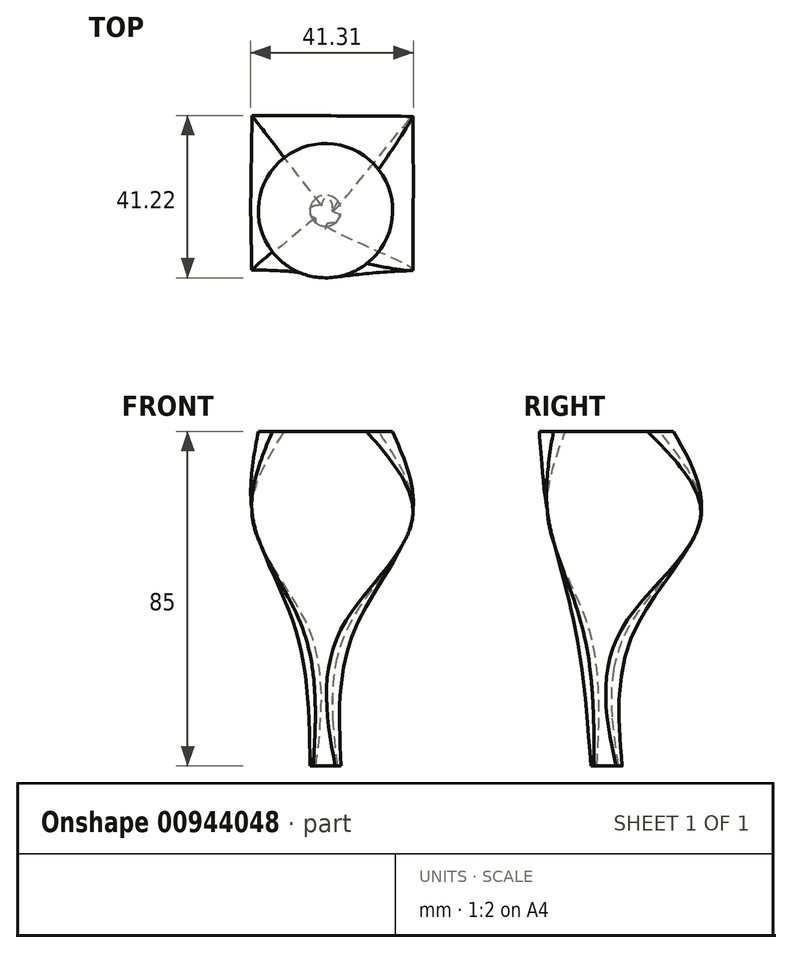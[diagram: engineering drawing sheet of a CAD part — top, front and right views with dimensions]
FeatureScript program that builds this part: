
annotation { "Feature Type Name" : "Feature", "Feature Type Description" : "" }
export const myFeature = defineFeature(function(context is Context, id is Id, definition is map)
    precondition{}
    {
        {
            var Q0;
            Q0=qCreatedBy(makeId("Top.planeOp"),FACE);
            var sketch = newSketch(context, id + "F0", { "sketchPlane" : qUnion([Q0])});
            skCircle(sketch, "E0", {"center": v(0, 0) * mm, "radius": 3.96 * mm});
            skSolve(sketch);
        }
        {
            var Q0;
            Q0=qCreatedBy(makeId("Top.planeOp"),FACE);
            cPlane(context, id + "F1", {"entities" : qUnion([Q0]), "cplaneType" : CPlaneType.OFFSET, "offset" : 85 * mm, "width" : 150 * mm, "height" : 150 * mm});
        }
        {
            var Q0;
            Q0=qCreatedBy(id+"F1.planeOp",FACE);
            var sketch = newSketch(context, id + "F2", { "sketchPlane" : qUnion([Q0])});
            skCircle(sketch, "E1", {"center": v(0, 0) * mm, "radius": 17.07 * mm});
            skSolve(sketch);
        }
        {
            var Q0;
            Q0=qCreatedBy(id+"F1.planeOp",FACE);
            cPlane(context, id + "F3", {"entities" : qUnion([Q0]), "cplaneType" : CPlaneType.OFFSET, "offset" : 20 * mm, "oppositeDirection" : true, "width" : 150 * mm, "height" : 150 * mm});
        }
        {
            var Q0;
            Q0=qCreatedBy(id+"F1.planeOp",FACE);
            cPlane(context, id + "F4", {"entities" : qUnion([Q0]), "cplaneType" : CPlaneType.OFFSET, "offset" : 48.2 * mm, "oppositeDirection" : true, "width" : 150 * mm, "height" : 150 * mm});
        }
        {
            var Q0;
            Q0=qCreatedBy(id+"F4.planeOp",FACE);
            var sketch = newSketch(context, id + "F5", { "sketchPlane" : qUnion([Q0])});
            skCircle(sketch, "E2", {"center": v(0, 0) * mm, "radius": 8.32 * mm});
            skSolve(sketch);
        }
        {
            var Q0;
            Q0=qCreatedBy(id+"F3.planeOp",FACE);
            var sketch = newSketch(context, id + "F6", { "sketchPlane" : qUnion([Q0])});
            skLineSegment(sketch, "E3", {"start": v(-18.72, 24.15) * mm, "end": v(-18.72, -15.03) * mm});
            skLineSegment(sketch, "E4", {"start": v(-18.72, -15.03) * mm, "end": v(22.2, -15.03) * mm});
            skLineSegment(sketch, "E5", {"start": v(22.2, -15.03) * mm, "end": v(22.2, 23.95) * mm});
            skLineSegment(sketch, "E6", {"start": v(22.2, 23.95) * mm, "end": v(-18.72, 24.15) * mm});
            skSolve(sketch);
        }
        {
            var Q0;
            Q0=makeQuery(id+"F0.imprint","IMPRINT",FACE,{"disambiguationData":[TD([[makeQuery(id+"F0.imprint","IMPRINT",EDGE,{"derivedFrom":sQuery(id+"F0.wireOp",EDGE,"E0")}),1.0]])]});
            var Q1;
            Q1=makeQuery(id+"F5.imprint","IMPRINT",FACE,{"disambiguationData":[TD([[makeQuery(id+"F5.imprint","IMPRINT",EDGE,{"derivedFrom":sQuery(id+"F5.wireOp",EDGE,"E2")}),1.0]])]});
            var Q2;
            Q2=makeQuery(id+"F6.imprint","IMPRINT",FACE,{"disambiguationData":[TD([[makeQuery(id+"F6.imprint","IMPRINT",EDGE,{"derivedFrom":sQuery(id+"F6.wireOp",EDGE,"E3")}),1.0]])]});
            var Q3;
            Q3=makeQuery(id+"F2.imprint","IMPRINT",FACE,{"disambiguationData":[TD([[makeQuery(id+"F2.imprint","IMPRINT",EDGE,{"derivedFrom":sQuery(id+"F2.wireOp",EDGE,"E1")}),1.0]])]});
            loft(context, id + "F7", {"sheetProfilesArray" : [{ "sheetProfileEntities" : qUnion([Q0]) }, { "sheetProfileEntities" : qUnion([Q1]) }, { "sheetProfileEntities" : qUnion([Q2]) }, { "sheetProfileEntities" : qUnion([Q3]) }]});
        }
    });
